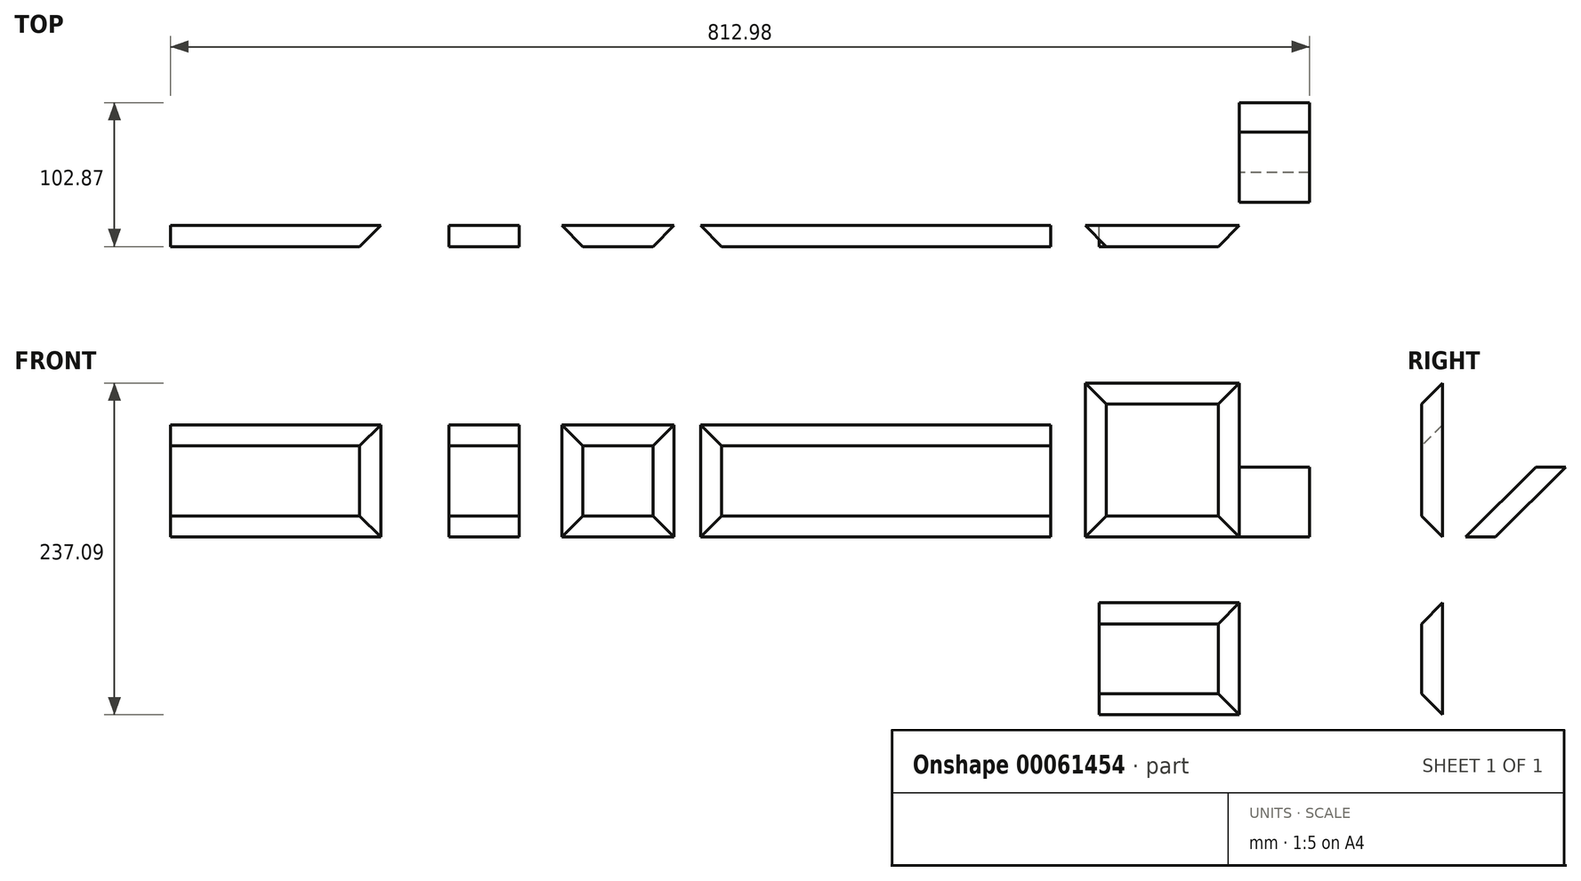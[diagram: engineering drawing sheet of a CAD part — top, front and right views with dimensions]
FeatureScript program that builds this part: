
annotation { "Feature Type Name" : "Feature", "Feature Type Description" : "" }
export const myFeature = defineFeature(function(context is Context, id is Id, definition is map)
    precondition{}
    {
        {
            var Q0;
            Q0=qCreatedBy(makeId("Front.planeOp"),FACE);
            var sketch = newSketch(context, id + "F0", { "sketchPlane" : qUnion([Q0])});
            skLineSegment(sketch, "E0.bottom", {"start": v(0, 0) * mm, "end": v(-110, 0) * mm});
            skLineSegment(sketch, "E0.top", {"start": v(0, 110) * mm, "end": v(-110, 110) * mm});
            skLineSegment(sketch, "E0.left", {"start": v(0, 0) * mm, "end": v(0, 110) * mm});
            skLineSegment(sketch, "E0.right", {"start": v(-110, 0) * mm, "end": v(-110, 110) * mm});
            skSolve(sketch);
        }
        {
            var Q0;
            Q0 = qSketchRegion(id + "F0", true);
            extrude(context, id + "F1", {"entities" : qUnion([Q0]), "depth" : 15 * mm});
        }
        {
            var Q0;
            Q0=qCreatedBy(makeId("Front.planeOp"),FACE);
            var sketch = newSketch(context, id + "F2", { "sketchPlane" : qUnion([Q0])});
            skLineSegment(sketch, "E1.bottom", {"start": v(-134.64, 0) * mm, "end": v(-384.64, 0) * mm});
            skLineSegment(sketch, "E1.top", {"start": v(-134.64, 80) * mm, "end": v(-384.64, 80) * mm});
            skLineSegment(sketch, "E1.left", {"start": v(-134.64, 0) * mm, "end": v(-134.64, 80) * mm});
            skLineSegment(sketch, "E1.right", {"start": v(-384.64, 0) * mm, "end": v(-384.64, 80) * mm});
            skSolve(sketch);
        }
        {
            var Q0;
            Q0 = qSketchRegion(id + "F2", true);
            extrude(context, id + "F3", {"entities" : qUnion([Q0]), "depth" : 15 * mm});
        }
        {
            var Q0;
            Q0=qCreatedBy(makeId("Front.planeOp"),FACE);
            var sketch = newSketch(context, id + "F4", { "sketchPlane" : qUnion([Q0])});
            skLineSegment(sketch, "E2.bottom", {"start": v(-403.57, 0) * mm, "end": v(-483.57, 0) * mm});
            skLineSegment(sketch, "E2.top", {"start": v(-403.57, 80) * mm, "end": v(-483.57, 80) * mm});
            skLineSegment(sketch, "E2.left", {"start": v(-403.57, 0) * mm, "end": v(-403.57, 80) * mm});
            skLineSegment(sketch, "E2.right", {"start": v(-483.57, 0) * mm, "end": v(-483.57, 80) * mm});
            skSolve(sketch);
        }
        {
            var Q0;
            Q0 = qSketchRegion(id + "F4", true);
            extrude(context, id + "F5", {"entities" : qUnion([Q0]), "depth" : 15 * mm});
        }
        {
            var Q0;
            Q0=qCreatedBy(makeId("Front.planeOp"),FACE);
            var sketch = newSketch(context, id + "F6", { "sketchPlane" : qUnion([Q0])});
            skLineSegment(sketch, "E3.bottom", {"start": v(-514.14, 0) * mm, "end": v(-564.14, 0) * mm});
            skLineSegment(sketch, "E3.top", {"start": v(-514.14, 80) * mm, "end": v(-564.14, 80) * mm});
            skLineSegment(sketch, "E3.left", {"start": v(-514.14, 0) * mm, "end": v(-514.14, 80) * mm});
            skLineSegment(sketch, "E3.right", {"start": v(-564.14, 0) * mm, "end": v(-564.14, 80) * mm});
            skSolve(sketch);
        }
        {
            var Q0;
            Q0 = qSketchRegion(id + "F6", true);
            extrude(context, id + "F7", {"entities" : qUnion([Q0]), "depth" : 15 * mm});
        }
        {
            var Q0;
            Q0=qCreatedBy(makeId("Front.planeOp"),FACE);
            var sketch = newSketch(context, id + "F8", { "sketchPlane" : qUnion([Q0])});
            skLineSegment(sketch, "E4.bottom", {"start": v(-612.98, 0) * mm, "end": v(-762.98, 0) * mm});
            skLineSegment(sketch, "E4.top", {"start": v(-612.98, 80) * mm, "end": v(-762.98, 80) * mm});
            skLineSegment(sketch, "E4.left", {"start": v(-612.98, 0) * mm, "end": v(-612.98, 80) * mm});
            skLineSegment(sketch, "E4.right", {"start": v(-762.98, 0) * mm, "end": v(-762.98, 80) * mm});
            skSolve(sketch);
        }
        {
            var Q0;
            Q0 = qSketchRegion(id + "F8", true);
            extrude(context, id + "F9", {"entities" : qUnion([Q0]), "depth" : 15 * mm});
        }
        {
            var Q0;
            Q0=qCreatedBy(makeId("Right.planeOp"),FACE);
            var sketch = newSketch(context, id + "F10", { "sketchPlane" : qUnion([Q0])});
            skLineSegment(sketch, "E5", {"start": v(16.66, 0) * mm, "end": v(37.87, 0) * mm});
            skLineSegment(sketch, "E6", {"start": v(37.87, 0) * mm, "end": v(87.87, 50) * mm});
            skLineSegment(sketch, "E7", {"start": v(87.87, 50) * mm, "end": v(66.66, 50) * mm});
            skLineSegment(sketch, "E8", {"start": v(66.66, 50) * mm, "end": v(16.66, 0) * mm});
            skSolve(sketch);
        }
        {
            var Q0;
            Q0 = qSketchRegion(id + "F10", true);
            extrude(context, id + "F11", {"entities" : qUnion([Q0]), "depth" : 50 * mm});
        }
        {
            var Q0;
            Q0=qCreatedBy(makeId("Front.planeOp"),FACE);
            var sketch = newSketch(context, id + "F12", { "sketchPlane" : qUnion([Q0])});
            skLineSegment(sketch, "E9.bottom", {"start": v(0, -47.09) * mm, "end": v(-100, -47.09) * mm});
            skLineSegment(sketch, "E9.top", {"start": v(0, -127.09) * mm, "end": v(-100, -127.09) * mm});
            skLineSegment(sketch, "E9.left", {"start": v(0, -47.09) * mm, "end": v(0, -127.09) * mm});
            skLineSegment(sketch, "E9.right", {"start": v(-100, -47.09) * mm, "end": v(-100, -127.09) * mm});
            skSolve(sketch);
        }
        {
            var Q0;
            Q0 = qSketchRegion(id + "F12", true);
            extrude(context, id + "F13", {"entities" : qUnion([Q0]), "depth" : 15 * mm});
        }
        {
            var Q0;
            Q0=makeQuery(id+"F5.opExtrude","CAP_FACE",FACE,{"disambiguationData":[OSD([sQuery(id+"F4.wireOp",EDGE,"E2.bottom"),sQuery(id+"F4.wireOp",EDGE,"E2.top"),sQuery(id+"F4.wireOp",EDGE,"E2.left"),sQuery(id+"F4.wireOp",EDGE,"E2.right")])],"isStart":false});
            var Q1;
            Q1=makeQuery(id+"F1.opExtrude","CAP_FACE",FACE,{"disambiguationData":[OSD([sQuery(id+"F0.wireOp",EDGE,"E0.bottom"),sQuery(id+"F0.wireOp",EDGE,"E0.top"),sQuery(id+"F0.wireOp",EDGE,"E0.left"),sQuery(id+"F0.wireOp",EDGE,"E0.right")])],"isStart":false});
            var Q2;
            Q2=makeQuery(id+"F3.opExtrude","CAP_EDGE",EDGE,{"disambiguationData":[OSD([sQuery(id+"F2.wireOp",EDGE,"E1.top")])],"isStart":false});
            var Q3;
            Q3=makeQuery(id+"F3.opExtrude","CAP_EDGE",EDGE,{"disambiguationData":[OSD([sQuery(id+"F2.wireOp",EDGE,"E1.right")])],"isStart":false});
            var Q4;
            Q4=makeQuery(id+"F3.opExtrude","CAP_EDGE",EDGE,{"disambiguationData":[OSD([sQuery(id+"F2.wireOp",EDGE,"E1.bottom")])],"isStart":false});
            var Q5;
            Q5=makeQuery(id+"F7.opExtrude","CAP_EDGE",EDGE,{"disambiguationData":[OSD([sQuery(id+"F6.wireOp",EDGE,"E3.top")])],"isStart":false});
            var Q6;
            Q6=makeQuery(id+"F7.opExtrude","CAP_EDGE",EDGE,{"disambiguationData":[OSD([sQuery(id+"F6.wireOp",EDGE,"E3.bottom")])],"isStart":false});
            var Q7;
            Q7=makeQuery(id+"F9.opExtrude","CAP_EDGE",EDGE,{"disambiguationData":[OSD([sQuery(id+"F8.wireOp",EDGE,"E4.bottom")])],"isStart":false});
            var Q8;
            Q8=makeQuery(id+"F9.opExtrude","CAP_EDGE",EDGE,{"disambiguationData":[OSD([sQuery(id+"F8.wireOp",EDGE,"E4.top")])],"isStart":false});
            var Q9;
            Q9=makeQuery(id+"F9.opExtrude","CAP_EDGE",EDGE,{"disambiguationData":[OSD([sQuery(id+"F8.wireOp",EDGE,"E4.left")])],"isStart":false});
            var Q10;
            Q10=makeQuery(id+"F13.opExtrude","CAP_EDGE",EDGE,{"disambiguationData":[OSD([sQuery(id+"F12.wireOp",EDGE,"E9.left")])],"isStart":false});
            var Q11;
            Q11=makeQuery(id+"F13.opExtrude","CAP_EDGE",EDGE,{"disambiguationData":[OSD([sQuery(id+"F12.wireOp",EDGE,"E9.bottom")])],"isStart":false});
            var Q12;
            Q12=makeQuery(id+"F13.opExtrude","CAP_EDGE",EDGE,{"disambiguationData":[OSD([sQuery(id+"F12.wireOp",EDGE,"E9.top")])],"isStart":false});
            chamfer(context, id + "F14", {"entities" : qUnion([Q0, Q1, Q2, Q3, Q4, Q5, Q6, Q7, Q8, Q9, Q10, Q11, Q12]), "width" : 15 * mm, "tangentPropagation" : true});
        }
    });
